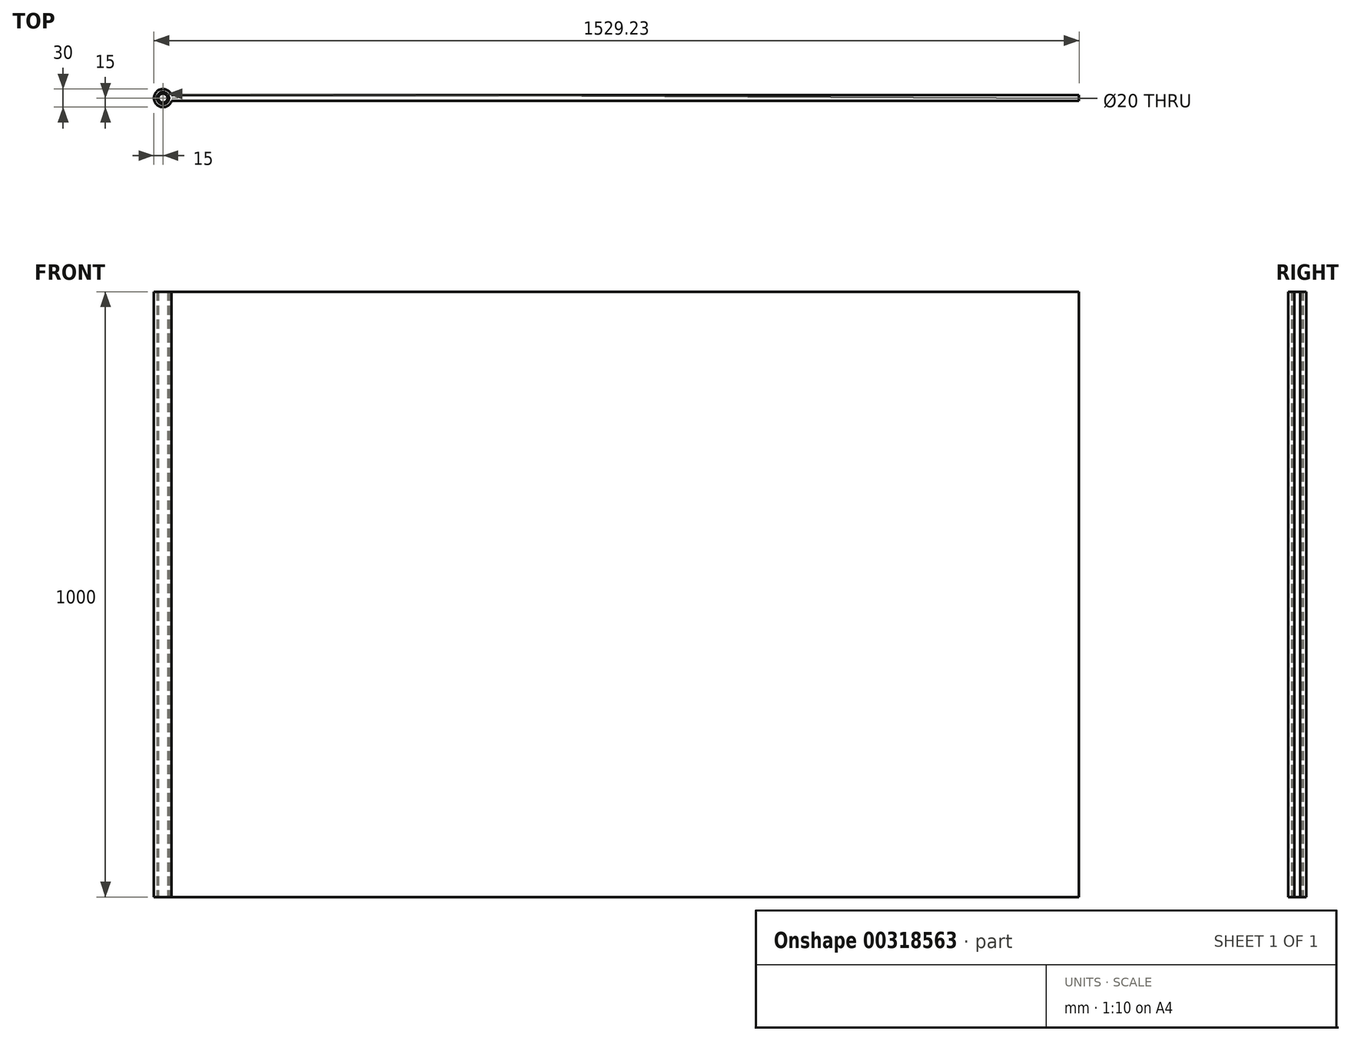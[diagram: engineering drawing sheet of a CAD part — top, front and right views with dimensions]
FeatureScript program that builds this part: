
annotation { "Feature Type Name" : "Feature", "Feature Type Description" : "" }
export const myFeature = defineFeature(function(context is Context, id is Id, definition is map)
    precondition{}
    {
        {
            var Q0;
            Q0=qCreatedBy(makeId("Top.planeOp"),FACE);
            var sketch = newSketch(context, id + "F0", { "sketchPlane" : qUnion([Q0])});
            skCircle(sketch, "E0", {"center": v(0, 0) * mm, "radius": 7.42 * mm});
            skSolve(sketch);
        }
        {
            var Q0;
            Q0 = qSketchRegion(id + "F0", true);
            extrude(context, id + "F1", {"entities" : qUnion([Q0]), "depth" : 1000 * mm, "offsetDistance" : 25 * mm});
        }
        {
            var Q0;
            Q0=qCreatedBy(makeId("Top.planeOp"),FACE);
            var sketch = newSketch(context, id + "F2", { "sketchPlane" : qUnion([Q0])});
            skCircle(sketch, "E1", {"center": v(0, 0) * mm, "radius": 10 * mm});
            skArc(sketch, "E2", {"start": v(14.23, 4.75) * mm, "mid": v(-15, 0) * mm, "end": v(14.23, -4.75) * mm});
            skLineSegment(sketch, "E3.bottom", {"start": v(14.23, 4.75) * mm, "end": v(1514.23, 4.75) * mm});
            skLineSegment(sketch, "E3.top", {"start": v(14.23, -4.75) * mm, "end": v(1514.23, -4.75) * mm});
            skLineSegment(sketch, "E3.right", {"start": v(1514.23, 4.75) * mm, "end": v(1514.23, -4.75) * mm});
            skPoint(sketch, "E4", {"position": v(1514.23, 0) * mm});
            skSolve(sketch);
        }
        {
            var Q0;
            Q0 = qSketchRegion(id + "F2", true);
            extrude(context, id + "F3", {"entities" : qUnion([Q0]), "depth" : 1000 * mm, "offsetDistance" : 25 * mm});
        }
    });
